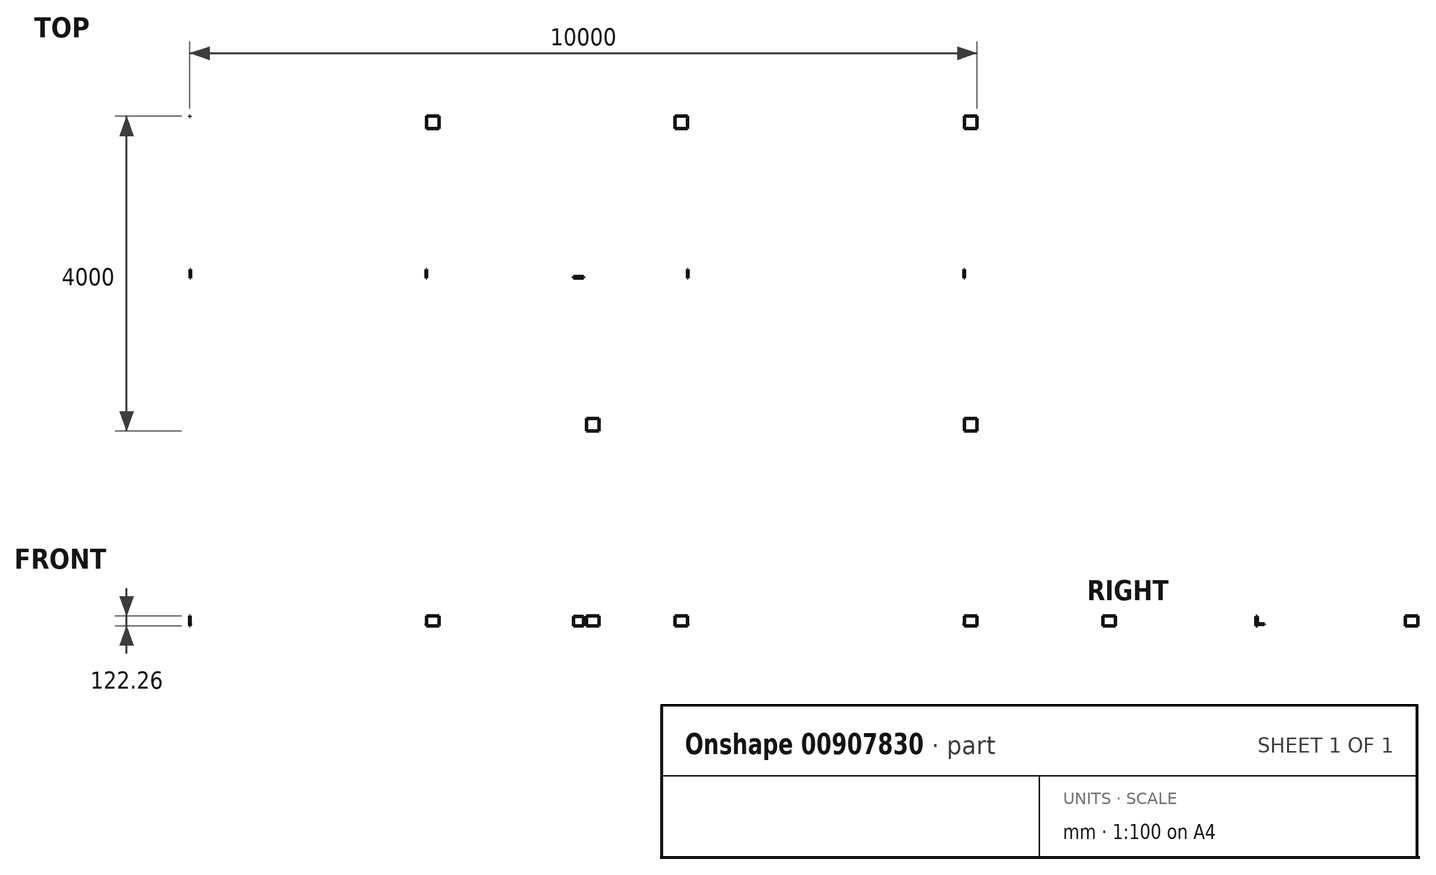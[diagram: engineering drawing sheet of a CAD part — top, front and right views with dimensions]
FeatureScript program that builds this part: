
annotation { "Feature Type Name" : "Feature", "Feature Type Description" : "" }
export const myFeature = defineFeature(function(context is Context, id is Id, definition is map)
    precondition{}
    {
        {
            var Q0;
            Q0=qCreatedBy(makeId("Top.planeOp"),FACE);
            var sketch = newSketch(context, id + "F0", { "sketchPlane" : qUnion([Q0])});
            skLineSegment(sketch, "E0.bottom", {"start": v(5000, 2000) * mm, "end": v(-5000, 2000) * mm});
            skLineSegment(sketch, "E0.top", {"start": v(5000, -2000) * mm, "end": v(-5000, -2000) * mm});
            skLineSegment(sketch, "E0.left", {"start": v(5000, 2000) * mm, "end": v(5000, -2000) * mm});
            skLineSegment(sketch, "E0.right", {"start": v(-5000, 2000) * mm, "end": v(-5000, -2000) * mm});
            skPoint(sketch, "E0.middle", {"position": v(0, 0) * mm});
            skSolve(sketch);
        }
        {
            var Q0;
            Q0=qCreatedBy(makeId("Top.planeOp"),FACE);
            var sketch = newSketch(context, id + "F1", { "sketchPlane" : qUnion([Q0])});
            skLineSegment(sketch, "E1.bottom", {"start": v(-127.21, -53.55) * mm, "end": v(-0.1, -53.55) * mm});
            skLineSegment(sketch, "E1.top", {"start": v(-127.21, -34.08) * mm, "end": v(-0.1, -34.08) * mm});
            skLineSegment(sketch, "E1.left", {"start": v(-127.21, -53.55) * mm, "end": v(-127.21, -34.08) * mm});
            skLineSegment(sketch, "E1.right", {"start": v(-0.1, -53.55) * mm, "end": v(-0.1, -34.08) * mm});
            skSolve(sketch);
        }
        {
            var Q0;
            Q0 = qSketchRegion(id + "F1", true);
            extrude(context, id + "F2", {"entities" : qUnion([Q0]), "depth" : 120.53 * mm, "offsetDistance" : 25.4 * mm});
        }
        {
            var Q0;
            Q0=qCreatedBy(makeId("Top.planeOp"),FACE);
            var sketch = newSketch(context, id + "F3", { "sketchPlane" : qUnion([Q0])});
            skLineSegment(sketch, "E2.bottom", {"start": v(-5000, 2000) * mm, "end": v(-4993.65, 2000) * mm});
            skLineSegment(sketch, "E2.top", {"start": v(-5000, 1994.44) * mm, "end": v(-4993.65, 1994.44) * mm});
            skLineSegment(sketch, "E2.left", {"start": v(-5000, 2000) * mm, "end": v(-5000, 1994.44) * mm});
            skLineSegment(sketch, "E2.right", {"start": v(-4993.65, 2000) * mm, "end": v(-4993.65, 1994.44) * mm});
            skLineSegment(sketch, "E3.bottom", {"start": v(-1993.65, 2000) * mm, "end": v(-1833.65, 2000) * mm});
            skLineSegment(sketch, "E3.top", {"start": v(-1993.65, 1840) * mm, "end": v(-1833.65, 1840) * mm});
            skLineSegment(sketch, "E3.left", {"start": v(-1993.65, 2000) * mm, "end": v(-1993.65, 1840) * mm});
            skLineSegment(sketch, "E3.right", {"start": v(-1833.65, 2000) * mm, "end": v(-1833.65, 1840) * mm});
            skLineSegment(sketch, "E4.bottom", {"start": v(1166.35, 2000) * mm, "end": v(1326.35, 2000) * mm});
            skLineSegment(sketch, "E4.top", {"start": v(1166.35, 1840) * mm, "end": v(1326.35, 1840) * mm});
            skLineSegment(sketch, "E4.left", {"start": v(1166.35, 2000) * mm, "end": v(1166.35, 1840) * mm});
            skLineSegment(sketch, "E4.right", {"start": v(1326.35, 2000) * mm, "end": v(1326.35, 1840) * mm});
            skLineSegment(sketch, "E5.bottom", {"start": v(5000, 2000) * mm, "end": v(4840, 2000) * mm});
            skLineSegment(sketch, "E5.top", {"start": v(5000, 1840) * mm, "end": v(4840, 1840) * mm});
            skLineSegment(sketch, "E5.left", {"start": v(5000, 2000) * mm, "end": v(5000, 1840) * mm});
            skLineSegment(sketch, "E5.right", {"start": v(4840, 2000) * mm, "end": v(4840, 1840) * mm});
            skLineSegment(sketch, "E6.bottom", {"start": v(5000, -2000) * mm, "end": v(4840, -2000) * mm});
            skLineSegment(sketch, "E6.top", {"start": v(5000, -1840) * mm, "end": v(4840, -1840) * mm});
            skLineSegment(sketch, "E6.left", {"start": v(5000, -2000) * mm, "end": v(5000, -1840) * mm});
            skLineSegment(sketch, "E6.right", {"start": v(4840, -2000) * mm, "end": v(4840, -1840) * mm});
            skLineSegment(sketch, "E7.bottom", {"start": v(198, -2000) * mm, "end": v(38, -2000) * mm});
            skLineSegment(sketch, "E7.top", {"start": v(198, -1840) * mm, "end": v(38, -1840) * mm});
            skLineSegment(sketch, "E7.left", {"start": v(198, -2000) * mm, "end": v(198, -1840) * mm});
            skLineSegment(sketch, "E7.right", {"start": v(38, -2000) * mm, "end": v(38, -1840) * mm});
            skSolve(sketch);
        }
        {
            var Q0;
            Q0 = qSketchRegion(id + "F3", true);
            extrude(context, id + "F4", {"entities" : qUnion([Q0]), "depth" : 122.26 * mm, "offsetDistance" : 25.4 * mm});
        }
        {
            var Q0;
            Q0=makeQuery(id+"F2.opExtrude","SWEPT_FACE",FACE,{"disambiguationData":[OSD([sQuery(id+"F1.wireOp",EDGE,"E1.bottom")])]});
            var sketch = newSketch(context, id + "F5", { "sketchPlane" : qUnion([Q0])});
            skLineSegment(sketch, "E8.bottom", {"start": v(4840, 15.24) * mm, "end": v(4833.65, 15.24) * mm});
            skLineSegment(sketch, "E8.top", {"start": v(4840, 21.6) * mm, "end": v(4833.65, 21.6) * mm});
            skLineSegment(sketch, "E8.left", {"start": v(4840, 15.24) * mm, "end": v(4840, 21.59) * mm});
            skLineSegment(sketch, "E8.right", {"start": v(4833.65, 15.24) * mm, "end": v(4833.65, 21.6) * mm});
            skLineSegment(sketch, "E9.bottom", {"start": v(1332.7, 15.24) * mm, "end": v(1326.35, 15.24) * mm});
            skLineSegment(sketch, "E9.top", {"start": v(1332.7, 21.6) * mm, "end": v(1326.35, 21.6) * mm});
            skLineSegment(sketch, "E9.left", {"start": v(1326.35, 15.24) * mm, "end": v(1326.35, 21.59) * mm});
            skLineSegment(sketch, "E9.right", {"start": v(1332.7, 15.24) * mm, "end": v(1332.7, 21.6) * mm});
            skLineSegment(sketch, "E10.bottom", {"start": v(-1993.65, 15.24) * mm, "end": v(-2000, 15.24) * mm});
            skLineSegment(sketch, "E10.top", {"start": v(-1993.65, 21.59) * mm, "end": v(-2000, 21.59) * mm});
            skLineSegment(sketch, "E10.left", {"start": v(-1993.65, 15.24) * mm, "end": v(-1993.65, 21.6) * mm});
            skLineSegment(sketch, "E10.right", {"start": v(-2000, 15.24) * mm, "end": v(-2000, 21.6) * mm});
            skLineSegment(sketch, "E11.bottom", {"start": v(-4993.65, 15.24) * mm, "end": v(-4987.3, 15.24) * mm});
            skLineSegment(sketch, "E11.top", {"start": v(-4993.65, 21.59) * mm, "end": v(-4987.3, 21.59) * mm});
            skLineSegment(sketch, "E11.left", {"start": v(-4993.65, 15.24) * mm, "end": v(-4993.65, 21.59) * mm});
            skLineSegment(sketch, "E11.right", {"start": v(-4987.3, 15.24) * mm, "end": v(-4987.3, 21.59) * mm});
            skSolve(sketch);
        }
        {
            var Q0;
            Q0 = qSketchRegion(id + "F5", true);
            extrude(context, id + "F6", {"entities" : qUnion([Q0]), "oppositeDirection" : true, "depth" : 107.04 * mm, "offsetDistance" : 25.4 * mm});
        }
    });
